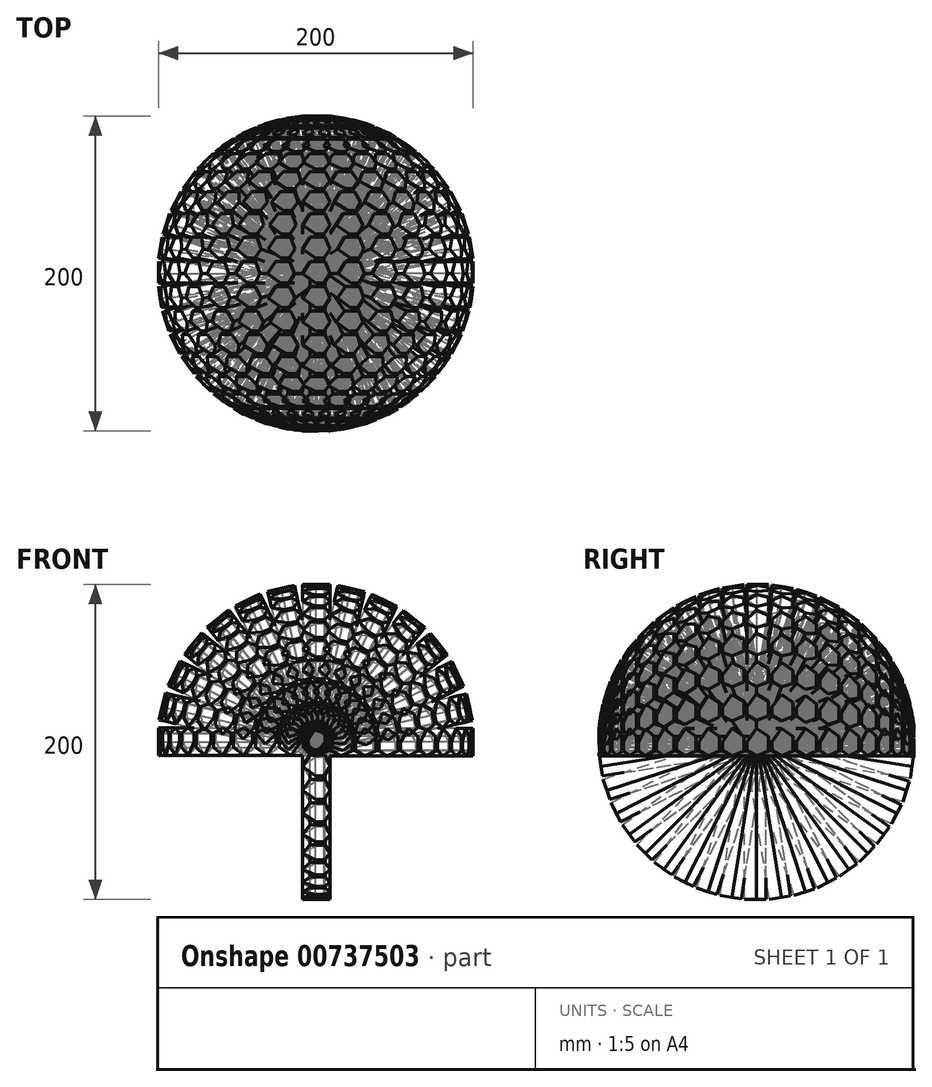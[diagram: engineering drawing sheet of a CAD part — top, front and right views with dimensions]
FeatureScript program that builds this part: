
annotation { "Feature Type Name" : "Feature", "Feature Type Description" : "" }
export const myFeature = defineFeature(function(context is Context, id is Id, definition is map)
    precondition{}
    {
        {
            var Q0;
            Q0=qCreatedBy(makeId("Top.planeOp"),FACE);
            var sketch = newSketch(context, id + "F0", { "sketchPlane" : qUnion([Q0])});
            skArc(sketch, "E0", {"start": v(94.67, 0) * mm, "mid": v(-0.33, 95.32) * mm, "end": v(-95.33, 0) * mm});
            skSolve(sketch);
        }
        {
            var Q0;
            Q0=qCreatedBy(makeId("Top.planeOp"),FACE);
            var sketch = newSketch(context, id + "F1", { "sketchPlane" : qUnion([Q0])});
            skLineSegment(sketch, "E1", {"start": v(-125, 0) * mm, "end": v(125, 0) * mm});
            skSolve(sketch);
        }
        {
            var Q0;
            Q0=sQuery(id+"F0.wireOp",EDGE,"E0");
            var Q1;
            Q1=sQuery(id+"F1.wireOp",EDGE,"E1");
            revolve(context, id + "F2", {"bodyType" : ToolBodyType.SURFACE, "surfaceOperationType" : NewSurfaceOperationType.NEW, "surfaceEntities" : qUnion([Q0]), "axis" : qUnion([Q1]), "revolveType" : RevolveType.ONE_DIRECTION, "angle" : 180 * degree});
        }
        {
            var Q0;
            Q0=qCreatedBy(makeId("Right.planeOp"),FACE);
            var sketch = newSketch(context, id + "F3", { "sketchPlane" : qUnion([Q0])});
            skLineSegment(sketch, "E2", {"start": v(39.26, 9.27) * mm, "end": v(43.26, 1.65) * mm});
            skLineSegment(sketch, "E3", {"start": v(43.26, 1.65) * mm, "end": v(40.12, 0) * mm});
            skLineSegment(sketch, "E4", {"start": v(40.12, 0) * mm, "end": v(41.26, 1.65) * mm});
            skLineSegment(sketch, "E5", {"start": v(41.26, 1.65) * mm, "end": v(39.26, 5.46) * mm});
            skLineSegment(sketch, "E6", {"start": v(39.26, 5.46) * mm, "end": v(37.26, 1.65) * mm});
            skLineSegment(sketch, "E7", {"start": v(37.26, 1.65) * mm, "end": v(38.12, 0) * mm});
            skLineSegment(sketch, "E8", {"start": v(38.12, 0) * mm, "end": v(35.26, 1.65) * mm});
            skLineSegment(sketch, "E9", {"start": v(35.26, 1.65) * mm, "end": v(39.26, 9.27) * mm});
            skSolve(sketch);
        }
        {
            var Q0;
            Q0 = qSketchRegion(id + "F3", true);
            extrude(context, id + "F4", {"entities" : qUnion([Q0]), "endBound" : BoundingType.SYMMETRIC, "depth" : 4 * mm, "offsetDistance" : 25 * mm});
        }
        {
            var Q0;
            Q0=qCreatedBy(makeId("Top.planeOp"),FACE);
            var sketch = newSketch(context, id + "F5", { "sketchPlane" : qUnion([Q0])});
            skLineSegment(sketch, "E10", {"start": v(-8.48, 0) * mm, "end": v(-3.5, 7.59) * mm});
            skLineSegment(sketch, "E11", {"start": v(-3.5, 7.59) * mm, "end": v(5.79, 7.59) * mm});
            skLineSegment(sketch, "E12", {"start": v(5.79, 7.59) * mm, "end": v(8.96, 0) * mm});
            skLineSegment(sketch, "E13", {"start": v(8.96, 0) * mm, "end": v(5.33, -6) * mm});
            skLineSegment(sketch, "E14", {"start": v(5.33, -6) * mm, "end": v(0, -6) * mm});
            skLineSegment(sketch, "E15", {"start": v(0, -6) * mm, "end": v(-8.48, 0) * mm});
            skSolve(sketch);
        }
        {
            var Q0;
            Q0 = qSketchRegion(id + "F5", true);
            extrude(context, id + "F6", {"entities" : qUnion([Q0]), "depth" : 100 * mm, "offsetDistance" : 25 * mm});
        }
        {
            var Q0;
            Q0=makeQuery(id+"F6.opExtrude","SWEPT_BODY",BODY,{"disambiguationData":[OSD([sQuery(id+"F5.wireOp",EDGE,"E10"),sQuery(id+"F5.wireOp",EDGE,"E11"),sQuery(id+"F5.wireOp",EDGE,"E12"),sQuery(id+"F5.wireOp",EDGE,"E13"),sQuery(id+"F5.wireOp",EDGE,"E14"),sQuery(id+"F5.wireOp",EDGE,"E15")])]});
            var Q1;
            Q1=makeQuery(id+"F2.opRevolve","SWEPT_FACE",FACE,{"disambiguationData":[OSD([sQuery(id+"F0.wireOp",EDGE,"E0")])]});
            circularPattern(context, id + "F7", {"entities" : qUnion([Q0]), "axis" : qUnion([Q1]), "angle" : 360 * degree, "instanceCount" : 40, "equalSpace" : true});
        }
        {
            var Q0;
            Q0=qCreatedBy(makeId("Top.planeOp"),FACE);
            var sketch = newSketch(context, id + "F8", { "sketchPlane" : qUnion([Q0])});
            skLineSegment(sketch, "E16", {"start": v(0, 114.64) * mm, "end": v(0, -128.09) * mm});
            skSolve(sketch);
        }
        {
            var Q0;
            Q0=makeQuery(id+"F7.opPattern","COPY",BODY,{"derivedFrom":makeQuery(id+"F6.opExtrude","SWEPT_BODY",BODY,{"disambiguationData":[OSD([sQuery(id+"F5.wireOp",EDGE,"E10"),sQuery(id+"F5.wireOp",EDGE,"E11"),sQuery(id+"F5.wireOp",EDGE,"E12"),sQuery(id+"F5.wireOp",EDGE,"E13"),sQuery(id+"F5.wireOp",EDGE,"E14"),sQuery(id+"F5.wireOp",EDGE,"E15")])]}),"instanceName":"30"});
            var Q1;
            Q1=makeQuery(id+"F7.opPattern","COPY",BODY,{"derivedFrom":makeQuery(id+"F6.opExtrude","SWEPT_BODY",BODY,{"disambiguationData":[OSD([sQuery(id+"F5.wireOp",EDGE,"E10"),sQuery(id+"F5.wireOp",EDGE,"E11"),sQuery(id+"F5.wireOp",EDGE,"E12"),sQuery(id+"F5.wireOp",EDGE,"E13"),sQuery(id+"F5.wireOp",EDGE,"E14"),sQuery(id+"F5.wireOp",EDGE,"E15")])]}),"instanceName":"31"});
            var Q2;
            Q2=makeQuery(id+"F7.opPattern","COPY",BODY,{"derivedFrom":makeQuery(id+"F6.opExtrude","SWEPT_BODY",BODY,{"disambiguationData":[OSD([sQuery(id+"F5.wireOp",EDGE,"E10"),sQuery(id+"F5.wireOp",EDGE,"E11"),sQuery(id+"F5.wireOp",EDGE,"E12"),sQuery(id+"F5.wireOp",EDGE,"E13"),sQuery(id+"F5.wireOp",EDGE,"E14"),sQuery(id+"F5.wireOp",EDGE,"E15")])]}),"instanceName":"32"});
            var Q3;
            Q3=makeQuery(id+"F7.opPattern","COPY",BODY,{"derivedFrom":makeQuery(id+"F6.opExtrude","SWEPT_BODY",BODY,{"disambiguationData":[OSD([sQuery(id+"F5.wireOp",EDGE,"E10"),sQuery(id+"F5.wireOp",EDGE,"E11"),sQuery(id+"F5.wireOp",EDGE,"E12"),sQuery(id+"F5.wireOp",EDGE,"E13"),sQuery(id+"F5.wireOp",EDGE,"E14"),sQuery(id+"F5.wireOp",EDGE,"E15")])]}),"instanceName":"33"});
            var Q4;
            Q4=makeQuery(id+"F7.opPattern","COPY",BODY,{"derivedFrom":makeQuery(id+"F6.opExtrude","SWEPT_BODY",BODY,{"disambiguationData":[OSD([sQuery(id+"F5.wireOp",EDGE,"E10"),sQuery(id+"F5.wireOp",EDGE,"E11"),sQuery(id+"F5.wireOp",EDGE,"E12"),sQuery(id+"F5.wireOp",EDGE,"E13"),sQuery(id+"F5.wireOp",EDGE,"E14"),sQuery(id+"F5.wireOp",EDGE,"E15")])]}),"instanceName":"34"});
            var Q5;
            Q5=makeQuery(id+"F7.opPattern","COPY",BODY,{"derivedFrom":makeQuery(id+"F6.opExtrude","SWEPT_BODY",BODY,{"disambiguationData":[OSD([sQuery(id+"F5.wireOp",EDGE,"E10"),sQuery(id+"F5.wireOp",EDGE,"E11"),sQuery(id+"F5.wireOp",EDGE,"E12"),sQuery(id+"F5.wireOp",EDGE,"E13"),sQuery(id+"F5.wireOp",EDGE,"E14"),sQuery(id+"F5.wireOp",EDGE,"E15")])]}),"instanceName":"35"});
            var Q6;
            Q6=makeQuery(id+"F7.opPattern","COPY",BODY,{"derivedFrom":makeQuery(id+"F6.opExtrude","SWEPT_BODY",BODY,{"disambiguationData":[OSD([sQuery(id+"F5.wireOp",EDGE,"E10"),sQuery(id+"F5.wireOp",EDGE,"E11"),sQuery(id+"F5.wireOp",EDGE,"E12"),sQuery(id+"F5.wireOp",EDGE,"E13"),sQuery(id+"F5.wireOp",EDGE,"E14"),sQuery(id+"F5.wireOp",EDGE,"E15")])]}),"instanceName":"36"});
            var Q7;
            Q7=makeQuery(id+"F7.opPattern","COPY",BODY,{"derivedFrom":makeQuery(id+"F6.opExtrude","SWEPT_BODY",BODY,{"disambiguationData":[OSD([sQuery(id+"F5.wireOp",EDGE,"E10"),sQuery(id+"F5.wireOp",EDGE,"E11"),sQuery(id+"F5.wireOp",EDGE,"E12"),sQuery(id+"F5.wireOp",EDGE,"E13"),sQuery(id+"F5.wireOp",EDGE,"E14"),sQuery(id+"F5.wireOp",EDGE,"E15")])]}),"instanceName":"37"});
            var Q8;
            Q8=makeQuery(id+"F7.opPattern","COPY",BODY,{"derivedFrom":makeQuery(id+"F6.opExtrude","SWEPT_BODY",BODY,{"disambiguationData":[OSD([sQuery(id+"F5.wireOp",EDGE,"E10"),sQuery(id+"F5.wireOp",EDGE,"E11"),sQuery(id+"F5.wireOp",EDGE,"E12"),sQuery(id+"F5.wireOp",EDGE,"E13"),sQuery(id+"F5.wireOp",EDGE,"E14"),sQuery(id+"F5.wireOp",EDGE,"E15")])]}),"instanceName":"38"});
            var Q9;
            Q9=makeQuery(id+"F7.opPattern","COPY",BODY,{"derivedFrom":makeQuery(id+"F6.opExtrude","SWEPT_BODY",BODY,{"disambiguationData":[OSD([sQuery(id+"F5.wireOp",EDGE,"E10"),sQuery(id+"F5.wireOp",EDGE,"E11"),sQuery(id+"F5.wireOp",EDGE,"E12"),sQuery(id+"F5.wireOp",EDGE,"E13"),sQuery(id+"F5.wireOp",EDGE,"E14"),sQuery(id+"F5.wireOp",EDGE,"E15")])]}),"instanceName":"39"});
            var Q10;
            Q10=makeQuery(id+"F6.opExtrude","SWEPT_BODY",BODY,{"disambiguationData":[OSD([sQuery(id+"F5.wireOp",EDGE,"E10"),sQuery(id+"F5.wireOp",EDGE,"E11"),sQuery(id+"F5.wireOp",EDGE,"E12"),sQuery(id+"F5.wireOp",EDGE,"E13"),sQuery(id+"F5.wireOp",EDGE,"E14"),sQuery(id+"F5.wireOp",EDGE,"E15")])]});
            var Q11;
            Q11=makeQuery(id+"F7.opPattern","COPY",BODY,{"derivedFrom":makeQuery(id+"F6.opExtrude","SWEPT_BODY",BODY,{"disambiguationData":[OSD([sQuery(id+"F5.wireOp",EDGE,"E10"),sQuery(id+"F5.wireOp",EDGE,"E11"),sQuery(id+"F5.wireOp",EDGE,"E12"),sQuery(id+"F5.wireOp",EDGE,"E13"),sQuery(id+"F5.wireOp",EDGE,"E14"),sQuery(id+"F5.wireOp",EDGE,"E15")])]}),"instanceName":"1"});
            var Q12;
            Q12=makeQuery(id+"F7.opPattern","COPY",BODY,{"derivedFrom":makeQuery(id+"F6.opExtrude","SWEPT_BODY",BODY,{"disambiguationData":[OSD([sQuery(id+"F5.wireOp",EDGE,"E10"),sQuery(id+"F5.wireOp",EDGE,"E11"),sQuery(id+"F5.wireOp",EDGE,"E12"),sQuery(id+"F5.wireOp",EDGE,"E13"),sQuery(id+"F5.wireOp",EDGE,"E14"),sQuery(id+"F5.wireOp",EDGE,"E15")])]}),"instanceName":"2"});
            var Q13;
            Q13=makeQuery(id+"F7.opPattern","COPY",BODY,{"derivedFrom":makeQuery(id+"F6.opExtrude","SWEPT_BODY",BODY,{"disambiguationData":[OSD([sQuery(id+"F5.wireOp",EDGE,"E10"),sQuery(id+"F5.wireOp",EDGE,"E11"),sQuery(id+"F5.wireOp",EDGE,"E12"),sQuery(id+"F5.wireOp",EDGE,"E13"),sQuery(id+"F5.wireOp",EDGE,"E14"),sQuery(id+"F5.wireOp",EDGE,"E15")])]}),"instanceName":"3"});
            var Q14;
            Q14=makeQuery(id+"F7.opPattern","COPY",BODY,{"derivedFrom":makeQuery(id+"F6.opExtrude","SWEPT_BODY",BODY,{"disambiguationData":[OSD([sQuery(id+"F5.wireOp",EDGE,"E10"),sQuery(id+"F5.wireOp",EDGE,"E11"),sQuery(id+"F5.wireOp",EDGE,"E12"),sQuery(id+"F5.wireOp",EDGE,"E13"),sQuery(id+"F5.wireOp",EDGE,"E14"),sQuery(id+"F5.wireOp",EDGE,"E15")])]}),"instanceName":"4"});
            var Q15;
            Q15=makeQuery(id+"F7.opPattern","COPY",BODY,{"derivedFrom":makeQuery(id+"F6.opExtrude","SWEPT_BODY",BODY,{"disambiguationData":[OSD([sQuery(id+"F5.wireOp",EDGE,"E10"),sQuery(id+"F5.wireOp",EDGE,"E11"),sQuery(id+"F5.wireOp",EDGE,"E12"),sQuery(id+"F5.wireOp",EDGE,"E13"),sQuery(id+"F5.wireOp",EDGE,"E14"),sQuery(id+"F5.wireOp",EDGE,"E15")])]}),"instanceName":"5"});
            var Q16;
            Q16=makeQuery(id+"F7.opPattern","COPY",BODY,{"derivedFrom":makeQuery(id+"F6.opExtrude","SWEPT_BODY",BODY,{"disambiguationData":[OSD([sQuery(id+"F5.wireOp",EDGE,"E10"),sQuery(id+"F5.wireOp",EDGE,"E11"),sQuery(id+"F5.wireOp",EDGE,"E12"),sQuery(id+"F5.wireOp",EDGE,"E13"),sQuery(id+"F5.wireOp",EDGE,"E14"),sQuery(id+"F5.wireOp",EDGE,"E15")])]}),"instanceName":"6"});
            var Q17;
            Q17=makeQuery(id+"F7.opPattern","COPY",BODY,{"derivedFrom":makeQuery(id+"F6.opExtrude","SWEPT_BODY",BODY,{"disambiguationData":[OSD([sQuery(id+"F5.wireOp",EDGE,"E10"),sQuery(id+"F5.wireOp",EDGE,"E11"),sQuery(id+"F5.wireOp",EDGE,"E12"),sQuery(id+"F5.wireOp",EDGE,"E13"),sQuery(id+"F5.wireOp",EDGE,"E14"),sQuery(id+"F5.wireOp",EDGE,"E15")])]}),"instanceName":"7"});
            var Q18;
            Q18=makeQuery(id+"F7.opPattern","COPY",BODY,{"derivedFrom":makeQuery(id+"F6.opExtrude","SWEPT_BODY",BODY,{"disambiguationData":[OSD([sQuery(id+"F5.wireOp",EDGE,"E10"),sQuery(id+"F5.wireOp",EDGE,"E11"),sQuery(id+"F5.wireOp",EDGE,"E12"),sQuery(id+"F5.wireOp",EDGE,"E13"),sQuery(id+"F5.wireOp",EDGE,"E14"),sQuery(id+"F5.wireOp",EDGE,"E15")])]}),"instanceName":"8"});
            var Q19;
            Q19=makeQuery(id+"F7.opPattern","COPY",BODY,{"derivedFrom":makeQuery(id+"F6.opExtrude","SWEPT_BODY",BODY,{"disambiguationData":[OSD([sQuery(id+"F5.wireOp",EDGE,"E10"),sQuery(id+"F5.wireOp",EDGE,"E11"),sQuery(id+"F5.wireOp",EDGE,"E12"),sQuery(id+"F5.wireOp",EDGE,"E13"),sQuery(id+"F5.wireOp",EDGE,"E14"),sQuery(id+"F5.wireOp",EDGE,"E15")])]}),"instanceName":"9"});
            var Q20;
            Q20=makeQuery(id+"F7.opPattern","COPY",BODY,{"derivedFrom":makeQuery(id+"F6.opExtrude","SWEPT_BODY",BODY,{"disambiguationData":[OSD([sQuery(id+"F5.wireOp",EDGE,"E10"),sQuery(id+"F5.wireOp",EDGE,"E11"),sQuery(id+"F5.wireOp",EDGE,"E12"),sQuery(id+"F5.wireOp",EDGE,"E13"),sQuery(id+"F5.wireOp",EDGE,"E14"),sQuery(id+"F5.wireOp",EDGE,"E15")])]}),"instanceName":"10"});
            var Q21;
            Q21=sQuery(id+"F8.wireOp",EDGE,"E16");
            circularPattern(context, id + "F9", {"entities" : qUnion([Q0, Q1, Q2, Q3, Q4, Q5, Q6, Q7, Q8, Q9, Q10, Q11, Q12, Q13, Q14, Q15, Q16, Q17, Q18, Q19, Q20]), "axis" : qUnion([Q21]), "angle" : 90 * degree, "instanceCount" : 8, "equalSpace" : true, "isCentered" : true});
        }
    });
